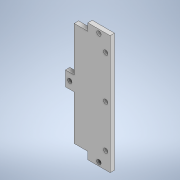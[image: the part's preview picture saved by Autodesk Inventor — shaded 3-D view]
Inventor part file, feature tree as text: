
AUTODESK INVENTOR PART (.ipt)
format: ipt  version: 2022 (Build 260153000, 153)  size: 138,752 bytes
history: native  units: in
note: dims shown in document units (in); Inventor stores cm internally (conversion verified against a paired STEP export)
features: extrude x3, sketch x3, projected_geometry x1
ambient origin geometry x8: Origin, YZ Plane, XZ Plane, XY Plane, X Axis, Y Axis, Z Axis, Center Point
bodies: Solid1 (feature_tree)
feature tree (7):
  extrude  "Extrusion1"  Depth=2.7953in
  extrude  "Extrusion2"  Depth=0.2362in
  extrude  "Extrusion3"  Depth=0.1181in
  sketch  "Sketch1"  dims[d0=0.7283in d1=2.7953in]
  sketch  "Sketch2"  dims[d2=0.1181in d3=0.0in d4=0.2362in]
  projected_geometry  "Projected Loop1"
  sketch  "Sketch3"  dims[d11=0.1181in d12=0.1181in d13=0.1181in d15=0.1969in d17=0.1181in d18=0.0in d19=0.2362in d20=0.1969in d21=0.1969in d22=0.1181in d23=0.1181in d24=0.0in]
